# Revit family: Kessel 28792 en
name_source: partatom
category: Plumbing Fixtures
revit_build: Autodesk Revit Architecture 2014 (Build: 20130308_1515(x64)
units: mm (PartAtom-declared; Revit-internal decimal feet)

## types (1)
- Kessel 28792 en
    <1.010.00.2> Number of the part of the guideline = 4
    <1.010.00.3> Issue date (month) of the guideline = 201410
    <1.010.00.4> Manufacturer name = Kessel
    <1.010.00.5> Revision date of the file = 20190228
    <1.800.00.3> BS number = 10000100000000000000000000000000000000000000000027000
    <1.800.00.4> Comment field = TeleControl modem
    <1.810.00.3> Manufacturer’s reference number = 28792
    <1.810.00.4> DATANORM number = 28792
    <1.810.00.6> GTIN number = 4026092066409
    <1.960/3L.00.8> Link (URL) = http://www.kessel.de
    <4.100.00.4> Area of application = Accessories
    <4.110.00.4> Model series = Accessories
    <4.700.00.10> Star / delta starting circuit with three-phase connection or three-phase current = no
    <4.700.00.46> vertical installation = no
    <4.700.00.47> outdoor installation = no
    <4.700.00.48> ATEX = no
    <4.700.00.49> protection class = protection class I
    <4.700.00.4> Product name = TeleControl modem
    <4.700.00.50> motor protection = no
    CONNECTOR0_DIAMETER_dZ_0r = 0 mm  [stored 0 ft]
    CONNECTOR0_dZ_00 = 39 mm
    CONNECTOR0_dZ_01 = 29 mm
    CONNECTOR0_ref_dX = 58 mm
    CONNECTOR0_ref_dY = 29 mm
    CONNECTOR0_ref_dZ = 29 mm
    CONNECTOR1_DIAMETER_dZ_0r = 0 mm  [stored 0 ft]
    CONNECTOR1_dZ_00 = 19 mm
    CONNECTOR1_dZ_01 = 9 mm
    CONNECTOR1_ref_dX = 24 mm
    CONNECTOR1_ref_dY = 29 mm
    CONNECTOR1_ref_dZ = 9 mm
    CONNECTOR2_DIAMETER_dZ_0r = 0 mm  [stored 0 ft]
    CONNECTOR2_dZ_01 = 10 mm  [stored 0.0328084 ft]
    CONNECTOR2_ref_dX = 10 mm  [stored 0.0328084 ft]
    CONNECTOR2_ref_dY = 29 mm
    CONNECTOR2_ref_dZ = 10 mm  [stored 0.0328084 ft]
    Manufacturer = Kessel
    Model = 28792
    URL = www.kessel.com

note: [stored X ft] marks values corroborated as IEEE doubles in the binary element streams (Revit-internal decimal feet)
